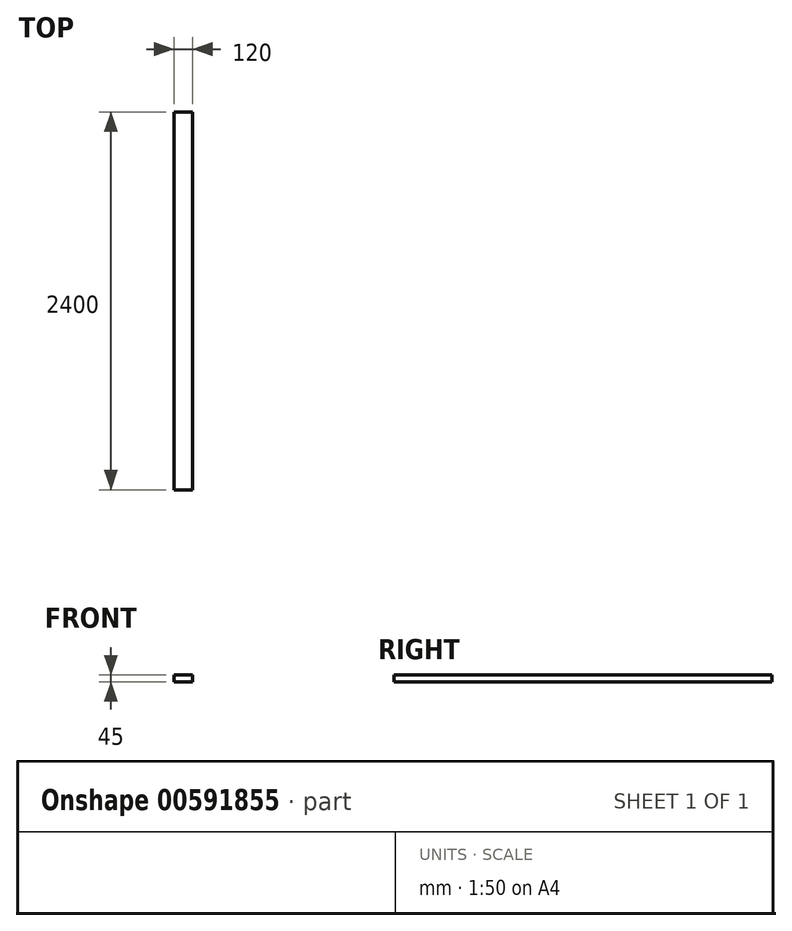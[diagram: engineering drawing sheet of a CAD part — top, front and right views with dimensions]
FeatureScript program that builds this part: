
annotation { "Feature Type Name" : "Feature", "Feature Type Description" : "" }
export const myFeature = defineFeature(function(context is Context, id is Id, definition is map)
    precondition{}
    {
        {
            var Q0;
            Q0=qCreatedBy(makeId("Top.planeOp"),FACE);
            var sketch = newSketch(context, id + "F0", { "sketchPlane" : qUnion([Q0])});
            skLineSegment(sketch, "E0.bottom", {"start": v(0, 0) * mm, "end": v(-120, 0) * mm});
            skLineSegment(sketch, "E0.top", {"start": v(0, 2400) * mm, "end": v(-120, 2400) * mm});
            skLineSegment(sketch, "E0.left", {"start": v(0, 0) * mm, "end": v(0, 2400) * mm});
            skLineSegment(sketch, "E0.right", {"start": v(-120, 0) * mm, "end": v(-120, 2400) * mm});
            skSolve(sketch);
        }
        {
            var Q0;
            Q0=makeQuery(id+"F0.imprint","IMPRINT",FACE,{"disambiguationData":[TD([[makeQuery(id+"F0.imprint","IMPRINT",EDGE,{"derivedFrom":sQuery(id+"F0.wireOp",EDGE,"E0.bottom")}),-1.0]])]});
            extrude(context, id + "F1", {"entities" : qUnion([Q0]), "depth" : 45 * mm, "offsetDistance" : 25 * mm});
        }
    });
